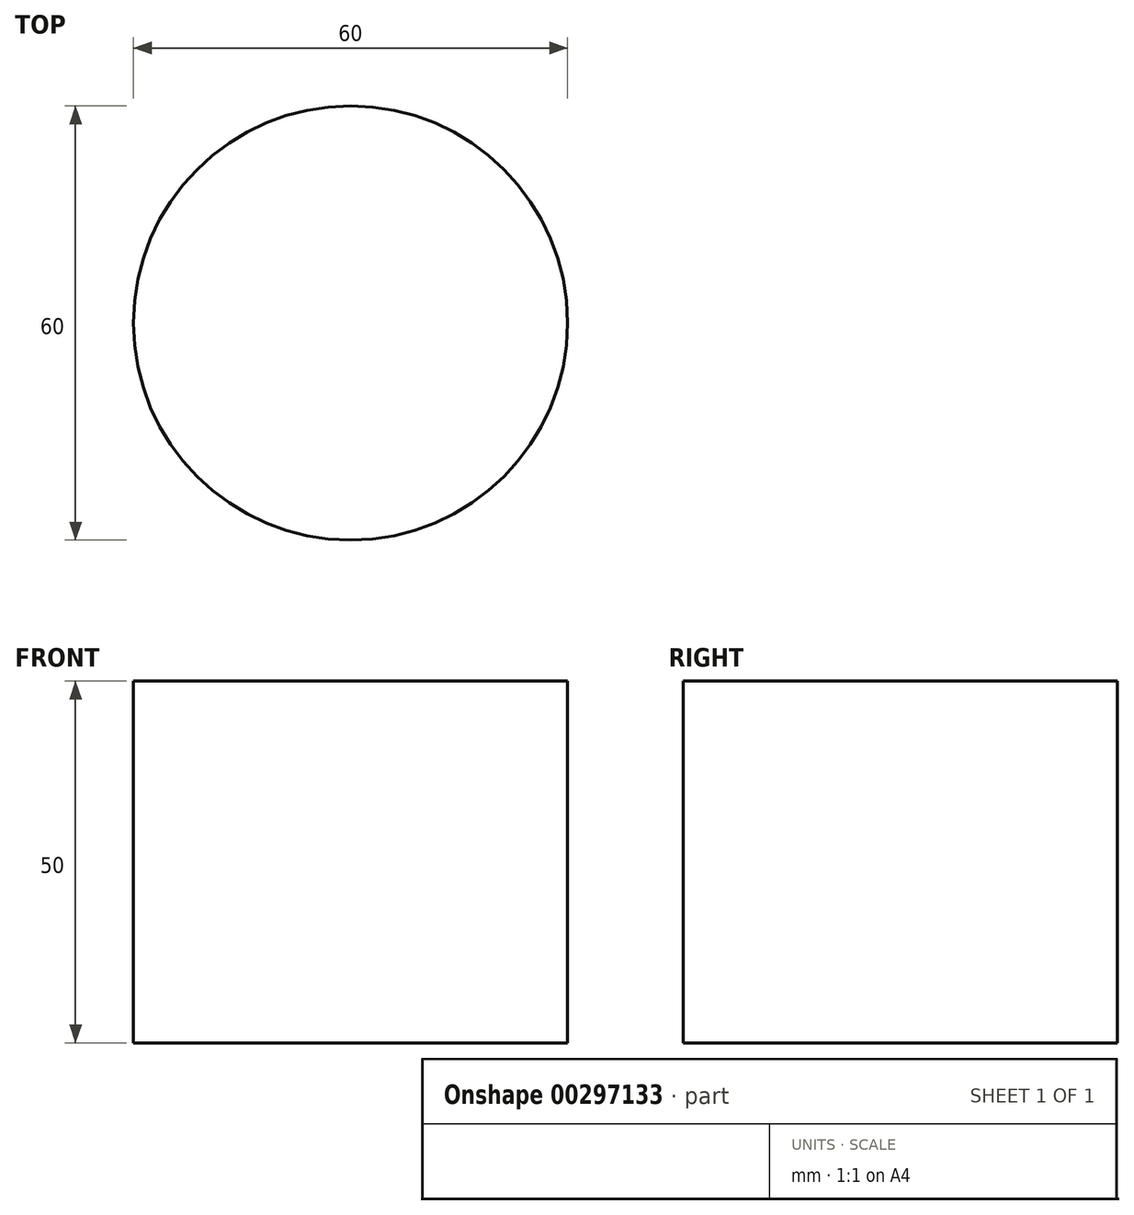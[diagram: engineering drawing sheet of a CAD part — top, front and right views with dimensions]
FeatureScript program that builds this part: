
annotation { "Feature Type Name" : "Feature", "Feature Type Description" : "" }
export const myFeature = defineFeature(function(context is Context, id is Id, definition is map)
    precondition{}
    {
        {
            var Q0;
            Q0=qCreatedBy(makeId("Front.planeOp"),FACE);
            var sketch = newSketch(context, id + "F0", { "sketchPlane" : qUnion([Q0])});
            skLineSegment(sketch, "E0.bottom", {"start": v(0, 0) * mm, "end": v(30, 0) * mm});
            skLineSegment(sketch, "E0.top", {"start": v(0, 50) * mm, "end": v(30, 50) * mm});
            skLineSegment(sketch, "E0.left", {"start": v(0, 0) * mm, "end": v(0, 50) * mm});
            skLineSegment(sketch, "E0.right", {"start": v(30, 0) * mm, "end": v(30, 50) * mm});
            skSolve(sketch);
        }
        {
            var Q0;
            Q0=makeQuery(id+"F0.imprint","IMPRINT",FACE,{"disambiguationData":[TD([[makeQuery(id+"F0.imprint","IMPRINT",EDGE,{"derivedFrom":sQuery(id+"F0.wireOp",EDGE,"E0.bottom")}),1.0]])]});
            var Q1;
            Q1=sQuery(id+"F0.wireOp",EDGE,"E0.left");
            revolve(context, id + "F1", {"entities" : qUnion([Q0]), "axis" : qUnion([Q1]), "revolveType" : RevolveType.FULL});
        }
    });
